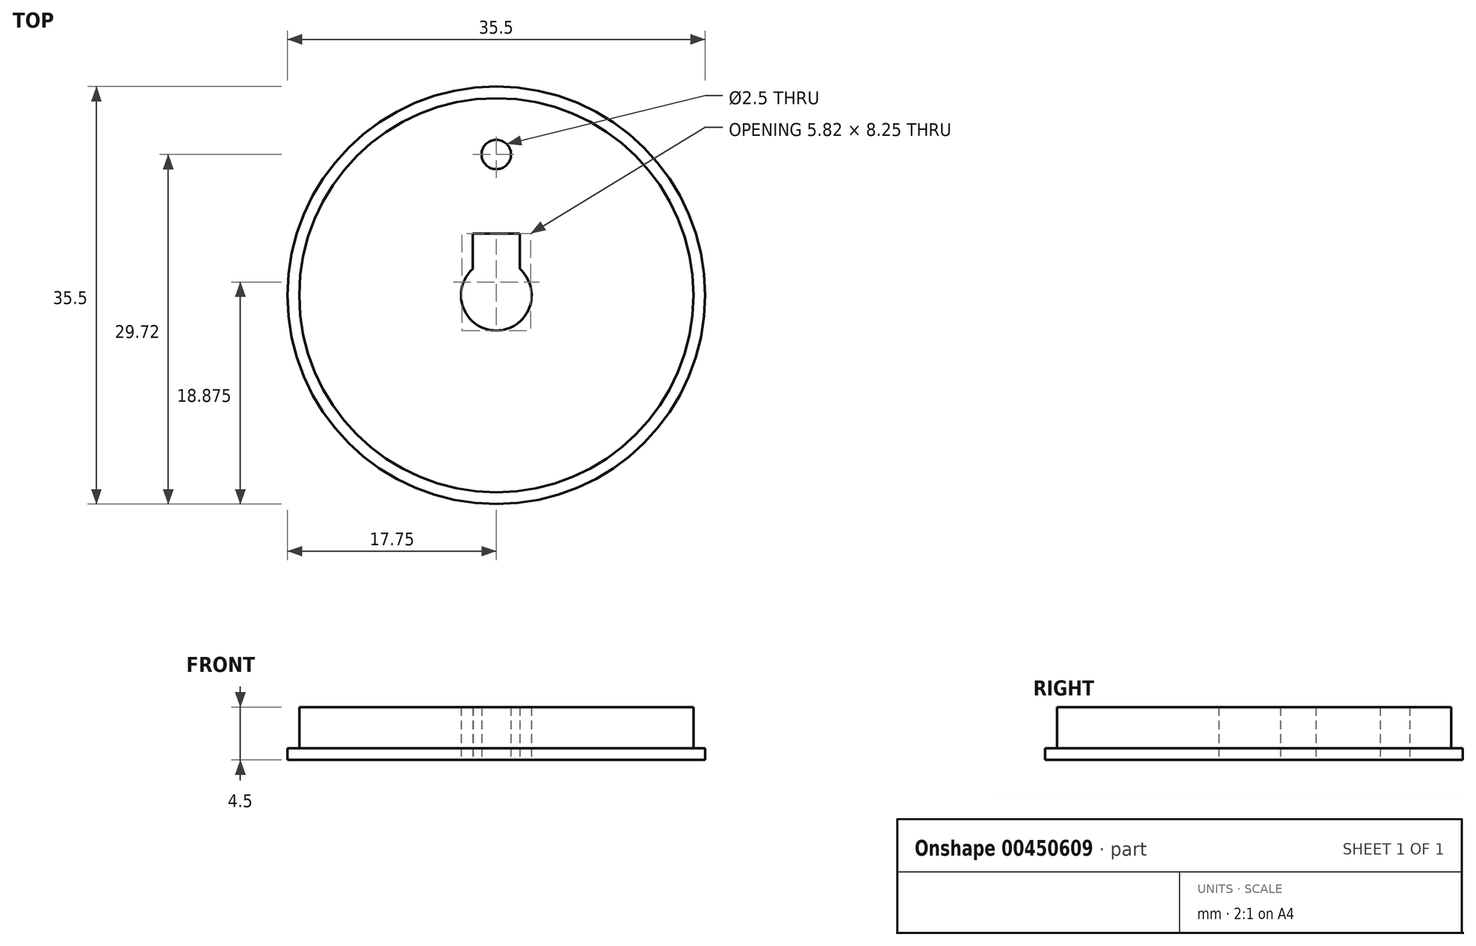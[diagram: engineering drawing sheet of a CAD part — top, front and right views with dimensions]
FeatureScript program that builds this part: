
annotation { "Feature Type Name" : "Feature", "Feature Type Description" : "" }
export const myFeature = defineFeature(function(context is Context, id is Id, definition is map)
    precondition{}
    {
        {
            var Q0;
            Q0=qCreatedBy(makeId("Top.planeOp"),FACE);
            var sketch = newSketch(context, id + "F0", { "sketchPlane" : qUnion([Q0])});
            skCircle(sketch, "E0", {"center": v(0, 0) * mm, "radius": 16.75 * mm});
            skCircle(sketch, "E1", {"center": v(0, 0) * mm, "radius": 17.75 * mm});
            skCircle(sketch, "E2", {"center": v(0, 0) * mm, "radius": 3 * mm});
            skLineSegment(sketch, "E3.bottom", {"start": v(2, 2.25) * mm, "end": v(-2, 2.25) * mm});
            skLineSegment(sketch, "E3.top", {"start": v(2, 5.25) * mm, "end": v(-2, 5.25) * mm});
            skLineSegment(sketch, "E3.left", {"start": v(2, 2.25) * mm, "end": v(2, 5.25) * mm});
            skLineSegment(sketch, "E3.right", {"start": v(-2, 2.25) * mm, "end": v(-2, 5.25) * mm});
            skPoint(sketch, "E3.middle", {"position": v(0, 3.75) * mm});
            skCircle(sketch, "E4", {"center": v(0, 11.97) * mm, "radius": 1.25 * mm});
            skSolve(sketch);
        }
        {
            var Q0;
            Q0=makeQuery(id+"F0.imprint","IMPRINT",FACE,{"disambiguationData":[TD([[makeQuery(id+"F0.imprint","IMPRINT",EDGE,{"derivedFrom":sQuery(id+"F0.wireOp",EDGE,"E0")}),1.0]])]});
            var Q1;
            Q1=makeQuery(id+"F0.imprint","IMPRINT",FACE,{"disambiguationData":[TD([[makeQuery(id+"F0.imprint","IMPRINT",EDGE,{"derivedFrom":sQuery(id+"F0.wireOp",EDGE,"b3465a21-8997-4f3d-873f-5268cfbf5236")}),1.0]])]});
            extrude(context, id + "F1", {"entities" : qUnion([Q0, Q1]), "depth" : 4.5 * mm});
        }
        {
            var Q0;
            Q0=makeQuery(id+"F0.imprint","IMPRINT",FACE,{"disambiguationData":[TD([[makeQuery(id+"F0.imprint","IMPRINT",EDGE,{"derivedFrom":sQuery(id+"F0.wireOp",EDGE,"E0")}),-1.0]])]});
            var Q1;
            Q1=makeQuery(id+"F0.imprint","IMPRINT",FACE,{"disambiguationData":[TD([[makeQuery(id+"F0.imprint","IMPRINT",EDGE,{"derivedFrom":sQuery(id+"F0.wireOp",EDGE,"b3465a21-8997-4f3d-873f-5268cfbf5236")}),-1.0]])]});
            extrude(context, id + "F2", {"entities" : qUnion([Q0, Q1]), "operationType" : NewBodyOperationType.ADD, "depth" : 1 * mm});
        }
    });
